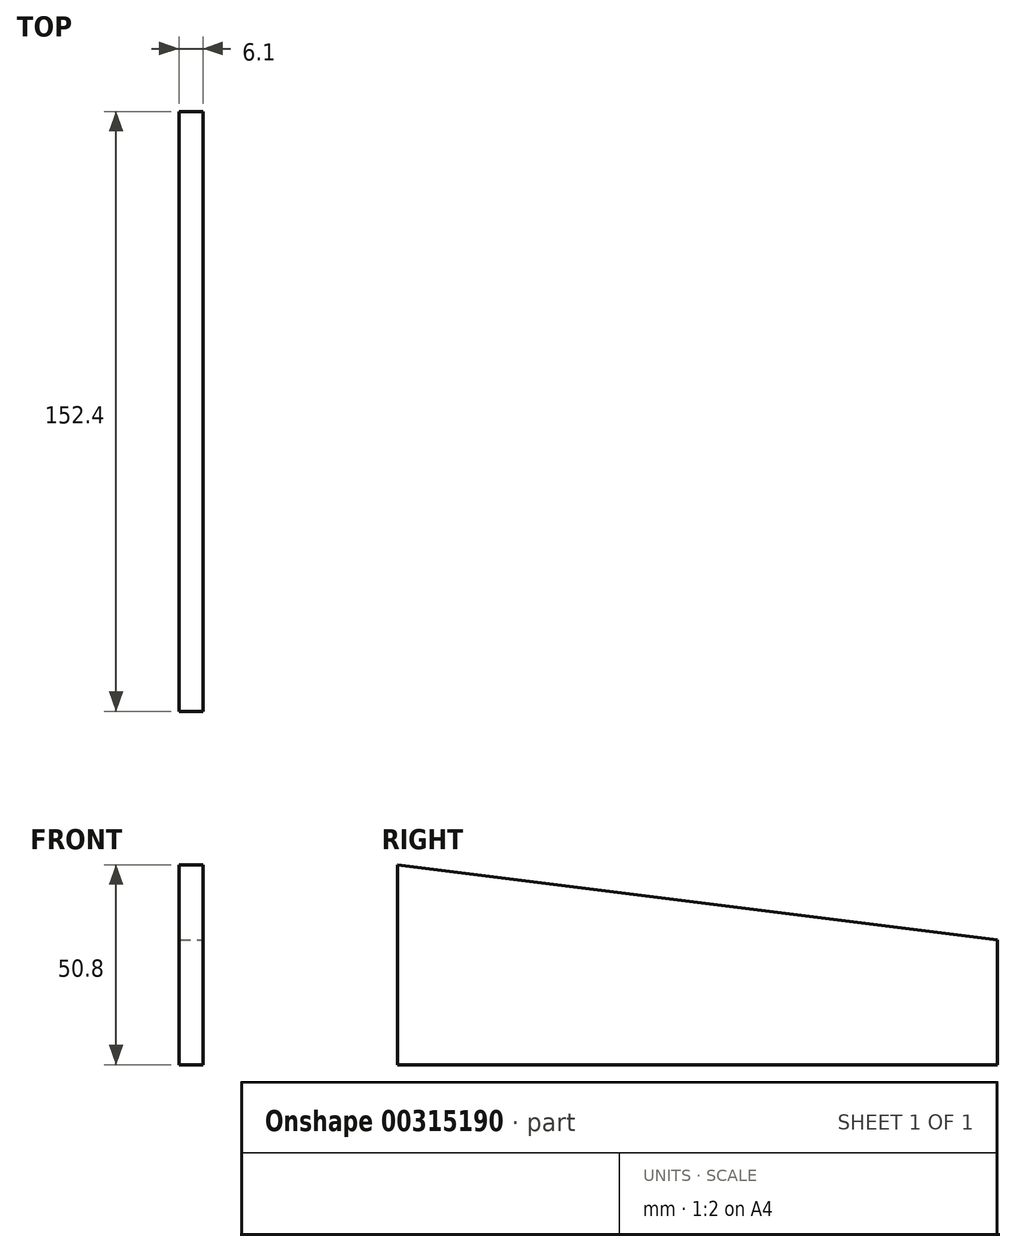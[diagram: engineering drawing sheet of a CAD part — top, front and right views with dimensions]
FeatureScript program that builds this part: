
annotation { "Feature Type Name" : "Feature", "Feature Type Description" : "" }
export const myFeature = defineFeature(function(context is Context, id is Id, definition is map)
    precondition{}
    {
        {
            var Q0;
            Q0=qCreatedBy(makeId("Right.planeOp"),FACE);
            var sketch = newSketch(context, id + "F0", { "sketchPlane" : qUnion([Q0])});
            skLineSegment(sketch, "E0", {"start": v(76.2, 0) * mm, "end": v(-76.2, 0) * mm});
            skLineSegment(sketch, "E1", {"start": v(-76.2, 0) * mm, "end": v(-76.2, 50.8) * mm});
            skLineSegment(sketch, "E2", {"start": v(-76.2, 50.8) * mm, "end": v(76.2, 31.75) * mm});
            skLineSegment(sketch, "E3", {"start": v(76.2, 31.75) * mm, "end": v(76.2, 0) * mm});
            skSolve(sketch);
        }
        {
            var Q0;
            Q0 = qSketchRegion(id + "F0", true);
            extrude(context, id + "F1", {"entities" : qUnion([Q0]), "oppositeDirection" : true, "depth" : 6.1 * mm});
        }
    });
